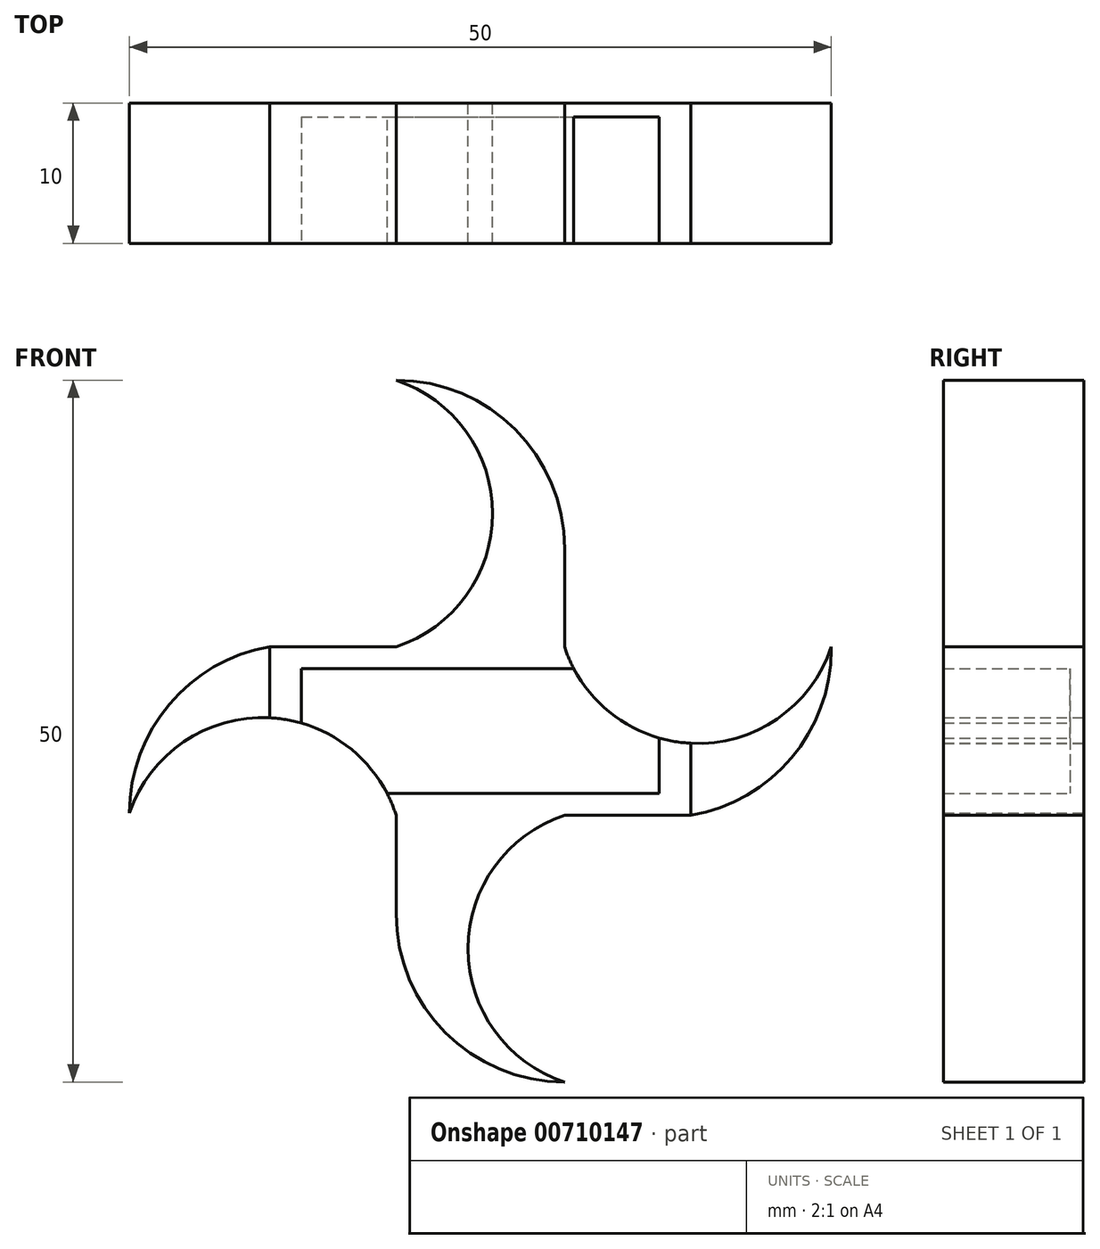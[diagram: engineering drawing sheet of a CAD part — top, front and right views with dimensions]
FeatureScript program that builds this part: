
annotation { "Feature Type Name" : "Feature", "Feature Type Description" : "" }
export const myFeature = defineFeature(function(context is Context, id is Id, definition is map)
    precondition{}
    {
        {
            var Q0;
            Q0=qCreatedBy(makeId("Top.planeOp"),FACE);
            var sketch = newSketch(context, id + "F0", { "sketchPlane" : qUnion([Q0])});
            skLineSegment(sketch, "E0", {"start": v(0, 0) * mm, "end": v(25.5, 0) * mm});
            skLineSegment(sketch, "E1", {"start": v(25.5, 0) * mm, "end": v(25.5, 8.9) * mm});
            skLineSegment(sketch, "E2", {"start": v(25.5, 8.9) * mm, "end": v(0, 8.9) * mm});
            skLineSegment(sketch, "E3", {"start": v(0, 8.9) * mm, "end": v(0, 0) * mm});
            skSolve(sketch);
        }
        {
            var Q0;
            Q0=makeQuery(id+"F0.imprint","IMPRINT",FACE,{"disambiguationData":[TD([[makeQuery(id+"F0.imprint","IMPRINT",EDGE,{"derivedFrom":sQuery(id+"F0.wireOp",EDGE,"E0")}),1.0]])]});
            extrude(context, id + "F1", {"entities" : qUnion([Q0]), "depth" : 8.9 * mm, "offsetDistance" : 25 * mm});
        }
        {
            var Q0;
            Q0=makeQuery(id+"F1.opExtrude","SWEPT_FACE",FACE,{"disambiguationData":[OSD([sQuery(id+"F0.wireOp",EDGE,"E0")])]});
            var sketch = newSketch(context, id + "F2", { "sketchPlane" : qUnion([Q0])});
            skLineSegment(sketch, "E4.bottom", {"start": v(-2.25, 10.45) * mm, "end": v(27.75, 10.45) * mm});
            skLineSegment(sketch, "E4.top", {"start": v(-2.25, -1.55) * mm, "end": v(27.75, -1.55) * mm});
            skLineSegment(sketch, "E4.left", {"start": v(-2.25, 10.45) * mm, "end": v(-2.25, -1.55) * mm});
            skLineSegment(sketch, "E4.right", {"start": v(27.75, 10.45) * mm, "end": v(27.75, -1.55) * mm});
            skPoint(sketch, "E4.middle", {"position": v(12.75, 4.45) * mm});
            skSolve(sketch);
        }
        {
            var Q0;
            {var subQ0=sQuery(id+"F0.wireOp",EDGE,"E0");Q0=makeQuery(id+"F2.imprint","IMPRINT",FACE,{"disambiguationData":[TD([[makeQuery(id+"F2.imprint","IMPRINT",EDGE,{"derivedFrom":makeQuery(id+"F1.opExtrude","CAP_EDGE",EDGE,{"disambiguationData":[OSD([subQ0])],"isStart":true})}),1.0]])]});}
            var Q1;
            Q1=makeQuery(id+"F2.imprint","IMPRINT",FACE,{"disambiguationData":[TD([[makeQuery(id+"F2.imprint","IMPRINT",EDGE,{"derivedFrom":sQuery(id+"F2.wireOp",EDGE,"E4.bottom")}),-1.0]])]});
            extrude(context, id + "F3", {"entities" : qUnion([Q0, Q1]), "oppositeDirection" : true, "depth" : 10 * mm, "offsetDistance" : 25 * mm});
        }
        {
            var Q0;
            Q0=makeQuery(id+"F1.opExtrude","SWEPT_FACE",FACE,{"disambiguationData":[OSD([sQuery(id+"F0.wireOp",EDGE,"E0")])]});
            extrude(context, id + "F4", {"entities" : qUnion([Q0]), "operationType" : NewBodyOperationType.REMOVE, "oppositeDirection" : true, "depth" : 9 * mm, "offsetDistance" : 25 * mm});
        }
        {
            var Q0;
            Q0=makeQuery(id+"F3.opExtrude","SWEPT_FACE",FACE,{"disambiguationData":[OSD([sQuery(id+"F2.wireOp",EDGE,"E4.left")])]});
            extrude(context, id + "F5", {"entities" : qUnion([Q0]), "depth" : 10 * mm, "offsetDistance" : 25 * mm});
        }
        {
            var Q0;
            Q0=makeQuery(id+"F3.opExtrude","SWEPT_FACE",FACE,{"disambiguationData":[OSD([sQuery(id+"F2.wireOp",EDGE,"E4.right")])]});
            extrude(context, id + "F6", {"entities" : qUnion([Q0]), "depth" : 10 * mm, "offsetDistance" : 25 * mm});
        }
        {
            var Q0;
            Q0=makeQuery(id+"F3.opExtrude","SWEPT_FACE",FACE,{"disambiguationData":[OSD([sQuery(id+"F2.wireOp",EDGE,"E4.bottom")])]});
            var sketch = newSketch(context, id + "F7", { "sketchPlane" : qUnion([Q0])});
            skLineSegment(sketch, "E5", {"start": v(12.75, 0) * mm, "end": v(18.75, 0) * mm});
            skLineSegment(sketch, "E6", {"start": v(18.75, 0) * mm, "end": v(18.75, 10) * mm});
            skLineSegment(sketch, "E7", {"start": v(18.75, 10) * mm, "end": v(12.75, 10) * mm});
            skLineSegment(sketch, "E8", {"start": v(12.75, 10) * mm, "end": v(6.75, 10) * mm});
            skLineSegment(sketch, "E9", {"start": v(6.75, 10) * mm, "end": v(6.75, 0) * mm});
            skLineSegment(sketch, "E10", {"start": v(12.75, 0) * mm, "end": v(6.75, 0) * mm});
            skSolve(sketch);
        }
        {
            var Q0;
            Q0=makeQuery(id+"F7.imprint","IMPRINT",FACE,{"disambiguationData":[TD([[makeQuery(id+"F7.imprint","IMPRINT",EDGE,{"derivedFrom":sQuery(id+"F7.wireOp",EDGE,"E5")}),1.0]])]});
            extrude(context, id + "F8", {"entities" : qUnion([Q0]), "operationType" : NewBodyOperationType.ADD, "depth" : 19 * mm, "offsetDistance" : 25 * mm});
        }
        {
            var Q0;
            Q0=makeQuery(id+"F3.opExtrude","SWEPT_FACE",FACE,{"disambiguationData":[OSD([sQuery(id+"F2.wireOp",EDGE,"E4.top")])]});
            var sketch = newSketch(context, id + "F9", { "sketchPlane" : qUnion([Q0])});
            skLineSegment(sketch, "E11", {"start": v(12.75, -10) * mm, "end": v(18.75, -10) * mm});
            skLineSegment(sketch, "E12", {"start": v(18.75, -10) * mm, "end": v(18.75, 0) * mm});
            skLineSegment(sketch, "E13", {"start": v(12.75, 0) * mm, "end": v(18.75, 0) * mm});
            skLineSegment(sketch, "E14", {"start": v(12.75, 0) * mm, "end": v(6.75, 0) * mm});
            skLineSegment(sketch, "E15", {"start": v(6.75, 0) * mm, "end": v(6.75, -10) * mm});
            skLineSegment(sketch, "E16", {"start": v(6.75, -10) * mm, "end": v(12.75, -10) * mm});
            skSolve(sketch);
        }
        {
            var Q0;
            Q0=makeQuery(id+"F9.imprint","IMPRINT",FACE,{"disambiguationData":[TD([[makeQuery(id+"F9.imprint","IMPRINT",EDGE,{"derivedFrom":sQuery(id+"F9.wireOp",EDGE,"E11")}),1.0]])]});
            extrude(context, id + "F10", {"entities" : qUnion([Q0]), "operationType" : NewBodyOperationType.ADD, "depth" : 19 * mm, "offsetDistance" : 25 * mm});
        }
        {
            var Q0;
            Q0=makeQuery(id+"F10.opExtrude","CAP_EDGE",EDGE,{"disambiguationData":[OSD([sQuery(id+"F9.wireOp",EDGE,"E15")])],"isStart":false});
            var Q1;
            Q1=makeQuery(id+"F5.opExtrude","CAP_EDGE",EDGE,{"disambiguationData":[OSD([sQuery(id+"F2.wireOp",EDGE,"E4.bottom"),sQuery(id+"F2.wireOp",EDGE,"E4.left")])],"isStart":false});
            var Q2;
            Q2=makeQuery(id+"F8.opExtrude","CAP_EDGE",EDGE,{"disambiguationData":[OSD([sQuery(id+"F7.wireOp",EDGE,"E6")])],"isStart":false});
            var Q3;
            Q3=makeQuery(id+"F6.opExtrude","CAP_EDGE",EDGE,{"disambiguationData":[OSD([sQuery(id+"F2.wireOp",EDGE,"E4.top"),sQuery(id+"F2.wireOp",EDGE,"E4.right")])],"isStart":false});
            fillet(context, id + "F11", {"entities" : qUnion([Q0, Q1, Q2, Q3]), "radius" : 12 * mm, "tangentPropagation" : true, "allowEdgeOverflow" : false});
        }
        {
            var Q0;
            Q0=makeQuery(id+"F10.boolean.opBoolean","MERGE",FACE,{"derivedFrom":[makeQuery(id+"F8.boolean.opBoolean","MERGE",FACE,{"derivedFrom":[makeQuery(id+"F3.opExtrude","CAP_FACE",FACE,{"disambiguationData":[OSD([sQuery(id+"F2.wireOp",EDGE,"E4.bottom"),sQuery(id+"F2.wireOp",EDGE,"E4.top"),sQuery(id+"F2.wireOp",EDGE,"E4.left"),sQuery(id+"F2.wireOp",EDGE,"E4.right")])],"isStart":false}),makeQuery(id+"F8.opExtrude","SWEPT_FACE",FACE,{"disambiguationData":[OSD([sQuery(id+"F7.wireOp",EDGE,"E7"),sQuery(id+"F7.wireOp",EDGE,"E8")])]})]}),makeQuery(id+"F10.opExtrude","SWEPT_FACE",FACE,{"disambiguationData":[OSD([sQuery(id+"F9.wireOp",EDGE,"E11"),sQuery(id+"F9.wireOp",EDGE,"E16")])]})]});
            var sketch = newSketch(context, id + "F12", { "sketchPlane" : qUnion([Q0])});
            skPoint(sketch, "E17.0", {"position": v(-12.75, 10.45) * mm});
            skLineSegment(sketch, "E18", {"start": v(-18.75, 10.45) * mm, "end": v(-18.75, -1.55) * mm});
            skLineSegment(sketch, "E19", {"start": v(-18.75, -1.55) * mm, "end": v(-6.75, -1.55) * mm});
            skLineSegment(sketch, "E20", {"start": v(-6.75, -1.55) * mm, "end": v(-6.75, 10.45) * mm});
            skLineSegment(sketch, "E21", {"start": v(-6.75, 10.45) * mm, "end": v(-18.75, 10.45) * mm});
            skLineSegment(sketch, "E22.0.0", {"start": v(12.25, -1.55) * mm, "end": v(12.25, -1.38) * mm});
            skArc(sketch, "E22.0.1", {"start": v(12.25, -1.38) * mm, "mid": v(9.42, 6.36) * mm, "end": v(2.25, 10.45) * mm});
            skLineSegment(sketch, "E22.0.2", {"start": v(2.25, 10.45) * mm, "end": v(2.25, -1.55) * mm});
            skLineSegment(sketch, "E22.0.3", {"start": v(2.25, -1.55) * mm, "end": v(12.25, -1.55) * mm});
            skLineSegment(sketch, "E23.0.0", {"start": v(-37.75, 10.45) * mm, "end": v(-37.75, 10.28) * mm});
            skArc(sketch, "E23.0.1", {"start": v(-37.75, 10.28) * mm, "mid": v(-34.92, 2.54) * mm, "end": v(-27.75, -1.55) * mm});
            skLineSegment(sketch, "E23.0.2", {"start": v(-27.75, -1.55) * mm, "end": v(-27.75, 10.45) * mm});
            skLineSegment(sketch, "E23.0.3", {"start": v(-27.75, 10.45) * mm, "end": v(-37.75, 10.45) * mm});
            skLineSegment(sketch, "E24.0.0", {"start": v(-18.75, -1.55) * mm, "end": v(-18.75, -20.55) * mm});
            skArc(sketch, "E24.0.1", {"start": v(-18.75, -20.55) * mm, "mid": v(-10.26, -17.04) * mm, "end": v(-6.75, -8.55) * mm});
            skLineSegment(sketch, "E24.0.2", {"start": v(-6.75, -8.55) * mm, "end": v(-6.75, -1.55) * mm});
            skLineSegment(sketch, "E24.0.3", {"start": v(-6.75, -1.55) * mm, "end": v(2.25, -1.55) * mm});
            skLineSegment(sketch, "E24.0.4", {"start": v(2.25, -1.55) * mm, "end": v(2.25, 10.45) * mm});
            skLineSegment(sketch, "E24.0.5", {"start": v(2.25, 10.45) * mm, "end": v(-6.75, 10.45) * mm});
            skLineSegment(sketch, "E24.0.6", {"start": v(-6.75, 10.45) * mm, "end": v(-6.75, 29.45) * mm});
            skArc(sketch, "E24.0.7", {"start": v(-6.75, 29.45) * mm, "mid": v(-15.24, 25.94) * mm, "end": v(-18.75, 17.45) * mm});
            skLineSegment(sketch, "E24.0.8", {"start": v(-18.75, 17.45) * mm, "end": v(-18.75, 10.45) * mm});
            skLineSegment(sketch, "E24.0.9", {"start": v(-18.75, 10.45) * mm, "end": v(-27.75, 10.45) * mm});
            skLineSegment(sketch, "E24.0.10", {"start": v(-27.75, 10.45) * mm, "end": v(-27.75, -1.55) * mm});
            skLineSegment(sketch, "E24.0.11", {"start": v(-27.75, -1.55) * mm, "end": v(-18.75, -1.55) * mm});
            skArc(sketch, "E25", {"start": v(-6.75, 29.45) * mm, "mid": v(-13.63, 19.95) * mm, "end": v(-6.75, 10.45) * mm});
            skArc(sketch, "E26", {"start": v(12.25, -1.38) * mm, "mid": v(2.69, 5.41) * mm, "end": v(-6.75, -1.55) * mm});
            skArc(sketch, "E27", {"start": v(-18.75, -20.55) * mm, "mid": v(-11.87, -11.05) * mm, "end": v(-18.75, -1.55) * mm});
            skArc(sketch, "E28", {"start": v(-37.75, 10.45) * mm, "mid": v(-28.25, 3.57) * mm, "end": v(-18.75, 10.45) * mm});
            skSolve(sketch);
        }
        {
            var Q0;
            {var subQ0=sQuery(id+"F12.wireOp",EDGE,"E23.0.3");Q0=makeQuery(id+"F12.imprint","IMPRINT",FACE,{"disambiguationData":[TD([[makeQuery(id+"F12.imprint","IMPRINT",EDGE,{"derivedFrom":subQ0}),1.0]])]});}
            var Q1;
            {var subQ0=sQuery(id+"F12.wireOp",EDGE,"E24.0.9");Q1=makeQuery(id+"F12.imprint","IMPRINT",FACE,{"disambiguationData":[TD([[makeQuery(id+"F12.imprint","IMPRINT",EDGE,{"derivedFrom":subQ0}),1.0]])]});}
            var Q2;
            Q2=makeQuery(id+"F12.imprint","IMPRINT",FACE,{"disambiguationData":[TD([[makeQuery(id+"F12.imprint","IMPRINT",EDGE,{"derivedFrom":sQuery(id+"F12.wireOp",EDGE,"E24.0.6")}),-1.0]])]});
            var Q3;
            {var subQ0=sQuery(id+"F12.wireOp",EDGE,"E22.0.0");Q3=makeQuery(id+"F12.imprint","IMPRINT",FACE,{"disambiguationData":[TD([[makeQuery(id+"F12.imprint","IMPRINT",EDGE,{"derivedFrom":subQ0}),1.0]])]});}
            var Q4;
            {var subQ0=sQuery(id+"F12.wireOp",EDGE,"E24.0.3");Q4=makeQuery(id+"F12.imprint","IMPRINT",FACE,{"disambiguationData":[TD([[makeQuery(id+"F12.imprint","IMPRINT",EDGE,{"derivedFrom":subQ0}),-1.0]])]});}
            var Q5;
            Q5=makeQuery(id+"F12.imprint","IMPRINT",FACE,{"disambiguationData":[TD([[makeQuery(id+"F12.imprint","IMPRINT",EDGE,{"derivedFrom":sQuery(id+"F12.wireOp",EDGE,"E24.0.0")}),-1.0]])]});
            extrude(context, id + "F13", {"entities" : qUnion([Q0, Q1, Q2, Q3, Q4, Q5]), "operationType" : NewBodyOperationType.REMOVE, "oppositeDirection" : true, "depth" : 10 * mm, "offsetDistance" : 25 * mm});
        }
    });
